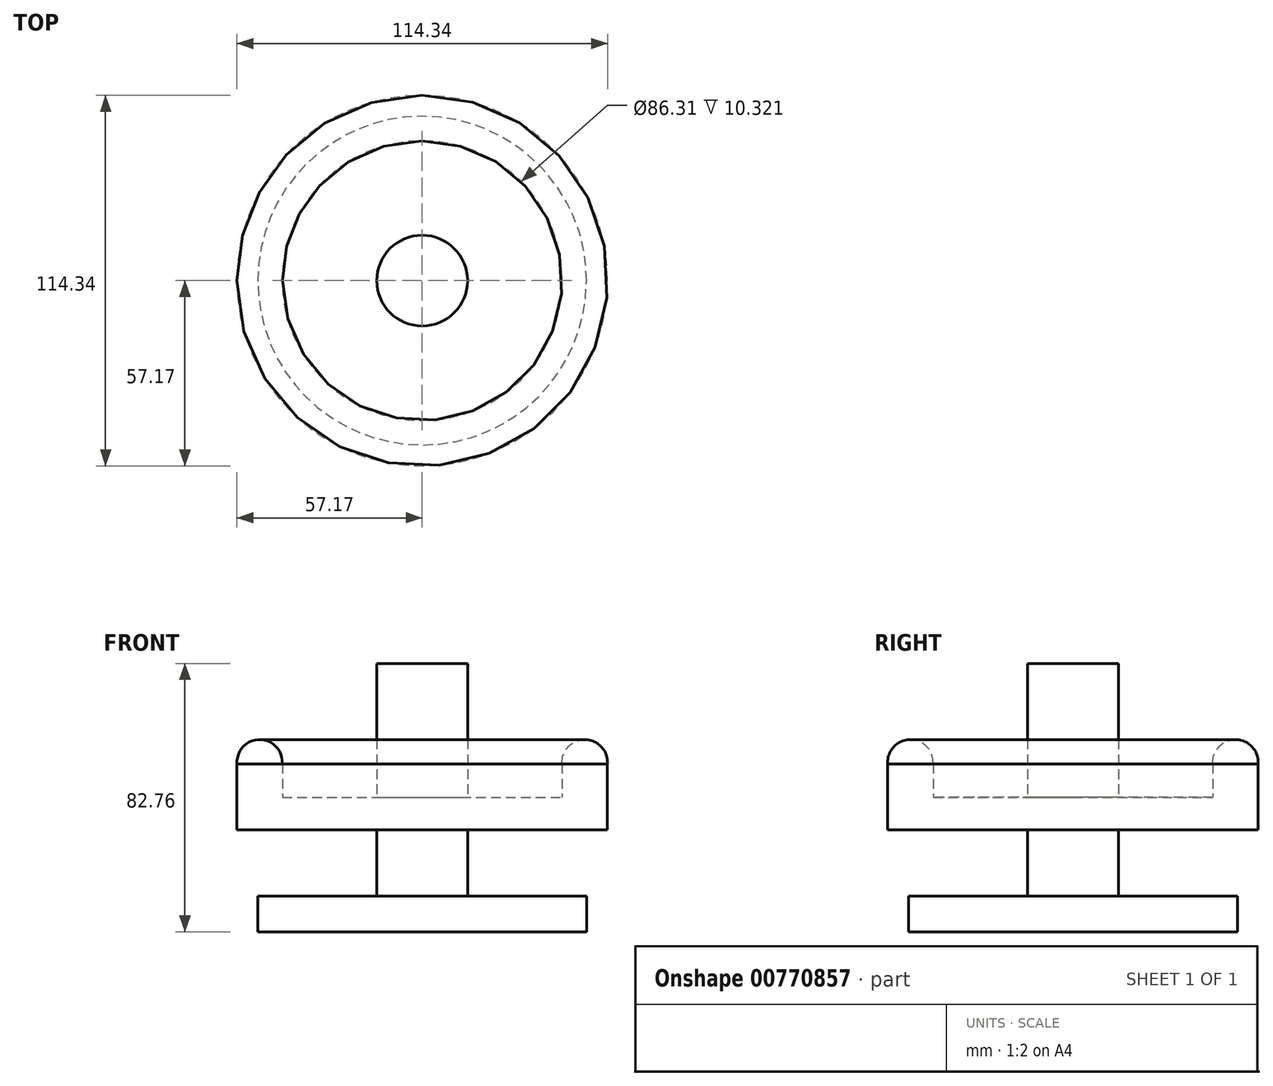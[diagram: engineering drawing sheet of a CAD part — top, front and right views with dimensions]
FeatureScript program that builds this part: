
annotation { "Feature Type Name" : "Feature", "Feature Type Description" : "" }
export const myFeature = defineFeature(function(context is Context, id is Id, definition is map)
    precondition{}
    {
        {
            var Q0;
            Q0=qCreatedBy(makeId("Front.planeOp"),FACE);
            var sketch = newSketch(context, id + "F0", { "sketchPlane" : qUnion([Q0])});
            skLineSegment(sketch, "E0.bottom", {"start": v(0, 0) * mm, "end": v(50.7, 0) * mm});
            skLineSegment(sketch, "E0.top", {"start": v(14, 11) * mm, "end": v(50.7, 11) * mm});
            skLineSegment(sketch, "E0.left", {"start": v(0, 0) * mm, "end": v(0, 11) * mm});
            skLineSegment(sketch, "E0.right", {"start": v(50.7, 0) * mm, "end": v(50.7, 11) * mm});
            skLineSegment(sketch, "E1.left", {"start": v(0, 11) * mm, "end": v(0, 53.74) * mm});
            skLineSegment(sketch, "E1.right", {"start": v(14, 11) * mm, "end": v(14, 31.48) * mm});
            skArc(sketch, "E2", {"start": v(14, 53.74) * mm, "mid": v(14.9, 54.62) * mm, "end": v(15.7, 55.6) * mm});
            skPoint(sketch, "E2.third.point", {"position": v(10.22, 71.93) * mm});
            skLineSegment(sketch, "E3.bottom", {"start": v(14, 41.48) * mm, "end": v(43.16, 41.48) * mm});
            skLineSegment(sketch, "E3.top", {"start": v(14, 31.48) * mm, "end": v(57.16, 31.48) * mm});
            skLineSegment(sketch, "E3.right", {"start": v(57.16, 41.48) * mm, "end": v(57.16, 31.48) * mm});
            skLineSegment(sketch, "E4.left", {"start": v(43.16, 41.48) * mm, "end": v(43.16, 51.8) * mm});
            skLineSegment(sketch, "E4.right", {"start": v(57.16, 41.48) * mm, "end": v(57.16, 51.8) * mm});
            skLineSegment(sketch, "E5.trimOffspring", {"start": v(14, 41.48) * mm, "end": v(14, 53.74) * mm});
            skLineSegment(sketch, "E6", {"start": v(0, 69.81) * mm, "end": v(0, 53.74) * mm});
            skArc(sketch, "E7", {"start": v(57.16, 51.8) * mm, "mid": v(50.16, 59.3) * mm, "end": v(43.16, 51.8) * mm});
            skPoint(sketch, "E7.third.point", {"position": v(44.98, 57.02) * mm});
            skLineSegment(sketch, "E8.right", {"start": v(14, 51.8) * mm, "end": v(14, 53.74) * mm});
            skPoint(sketch, "E9.orphan", {"position": v(14, 63.23) * mm});
            skLineSegment(sketch, "E10", {"start": v(0, 69.81) * mm, "end": v(0, 104.6) * mm});
            skLineSegment(sketch, "E11", {"start": v(14, 51.8) * mm, "end": v(14, 100) * mm});
            skArc(sketch, "E12", {"start": v(0, 104.6) * mm, "mid": v(20.93, 101.04) * mm, "end": v(36.26, 115.74) * mm});
            skLineSegment(sketch, "E13", {"start": v(0, 104.6) * mm, "end": v(0, 142.61) * mm});
            skLineSegment(sketch, "E14", {"start": v(36.26, 115.74) * mm, "end": v(120.08, 131.53) * mm});
            skLineSegment(sketch, "E15", {"start": v(120.08, 131.53) * mm, "end": v(36.24, 131.53) * mm});
            skArc(sketch, "E16.trimOffspring", {"start": v(36.24, 131.53) * mm, "mid": v(20.9, 146.18) * mm, "end": v(0, 142.61) * mm});
            skLineSegment(sketch, "E17.bottom", {"start": v(-35.67, 174.3) * mm, "end": v(124.53, 174.3) * mm});
            skLineSegment(sketch, "E17.top", {"start": v(-35.67, 82.76) * mm, "end": v(124.53, 82.76) * mm});
            skLineSegment(sketch, "E17.left", {"start": v(-35.67, 174.3) * mm, "end": v(-35.67, 82.76) * mm});
            skLineSegment(sketch, "E17.right", {"start": v(124.53, 174.3) * mm, "end": v(124.53, 82.76) * mm});
            skSolve(sketch);
        }
        {
            var Q0;
            Q0=makeQuery(id+"F0.imprint","IMPRINT",FACE,{"disambiguationData":[TD([[makeQuery(id+"F0.imprint","IMPRINT",EDGE,{"derivedFrom":sQuery(id+"F0.wireOp",EDGE,"E0.bottom")}),1.0]])]});
            var Q1;
            Q1=sQuery(id+"F0.wireOp",EDGE,"E1.left");
            revolve(context, id + "F1", {"surfaceOperationType" : NewSurfaceOperationType.NEW, "entities" : qUnion([Q0]), "axis" : qUnion([Q1]), "revolveType" : RevolveType.FULL});
        }
    });
